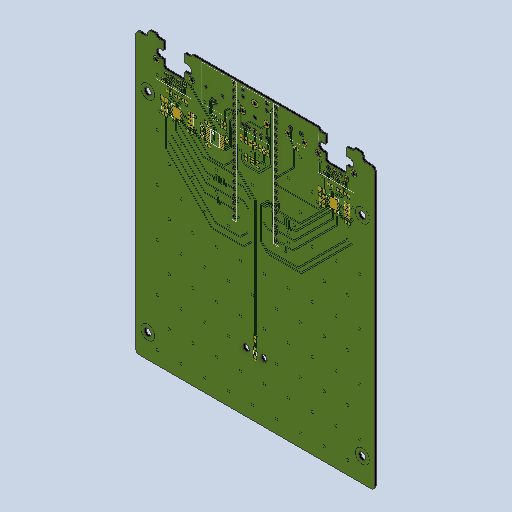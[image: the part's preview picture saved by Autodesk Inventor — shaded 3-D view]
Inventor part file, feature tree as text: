
AUTODESK INVENTOR PART (.ipt)
format: ipt  version: 2022.2 (Build 262287010, 287A)  size: 1,563,136 bytes
history: native  units: mm
features: hole x93, sketch x93, other x8, extrude x3
ambient origin geometry x8: Origin, YZ Plane, XZ Plane, XY Plane, X Axis, Y Axis, Z Axis, Center Point
bodies: Solid1 (feature_tree)
feature tree (197):
  other  "BaseBoard_BOARD"
  other  "BoardFrontPlane"
  extrude  "BoardOutline"  Depth=0.13mm TaperAngle=0.0deg
  hole  "J4-1"  [1 undecoded]
  hole  "J4-2"  [1 undecoded]
  hole  "J4-3"  [1 undecoded]
  hole  "J4-4"  [1 undecoded]
  hole  "J4-5"  [1 undecoded]
  hole  "J4-6"  [1 undecoded]
  hole  "J2-21"  [1 undecoded]
  hole  "J2-22"  [1 undecoded]
  hole  "J2-23"  [1 undecoded]
  hole  "J2-24"  [1 undecoded]
  hole  "J2-25"  [1 undecoded]
  hole  "J2-26"  [1 undecoded]
  hole  "J2-27"  [1 undecoded]
  hole  "J2-28"  [1 undecoded]
  hole  "J2-29"  [1 undecoded]
  hole  "J2-30"  [1 undecoded]
  hole  "J2-31"  [1 undecoded]
  hole  "J2-32"  [1 undecoded]
  hole  "J2-33"  [1 undecoded]
  hole  "J2-34"  [1 undecoded]
  hole  "J2-35"  [1 undecoded]
  hole  "J2-36"  [1 undecoded]
  hole  "J2-37"  [1 undecoded]
  hole  "J2-38"  [1 undecoded]
  hole  "J2-39"  [1 undecoded]
  hole  "J2-40"  [1 undecoded]
  hole  "J1-1"  [1 undecoded]
  hole  "J1-2"  [1 undecoded]
  hole  "J1-3"  [1 undecoded]
  hole  "J1-4"  [1 undecoded]
  hole  "J1-5"  [1 undecoded]
  hole  "J1-6"  [1 undecoded]
  hole  "J1-7"  [1 undecoded]
  hole  "J1-8"  [1 undecoded]
  hole  "J1-9"  [1 undecoded]
  hole  "J1-10"  [1 undecoded]
  hole  "J1-11"  [1 undecoded]
  hole  "J1-12"  [1 undecoded]
  hole  "J1-13"  [1 undecoded]
  hole  "J1-14"  [1 undecoded]
  hole  "J1-15"  [1 undecoded]
  hole  "J1-16"  [1 undecoded]
  hole  "J1-17"  [1 undecoded]
  hole  "J1-18"  [1 undecoded]
  hole  "J1-19"  [1 undecoded]
  hole  "J1-20"  [1 undecoded]
  extrude  "Cutout 1"  [1 undecoded]
  extrude  "Cutout 2"  [1 undecoded]
  other  "Decal_Top"
  other  "Decal_Bottom"
  hole  "J3-MH7"  [1 undecoded]
  hole  "J3-MH5"  [1 undecoded]
  hole  "J3-MH6"  [1 undecoded]
  hole  "J3-MH4"  [1 undecoded]
  hole  "J3-MH3"  [1 undecoded]
  hole  "J3-MH2"  [1 undecoded]
  hole  "J3-MH1"  [1 undecoded]
  hole  "J3-1"  [1 undecoded]
  hole  "J3-4"  [1 undecoded]
  hole  "J3-5"  [1 undecoded]
  hole  "J3-6"  [1 undecoded]
  hole  "J3-2"  [1 undecoded]
  hole  "J3-3"  [1 undecoded]
  hole  "J6-MH4"  [1 undecoded]
  hole  "J6-MH3"  [1 undecoded]
  hole  "J6-MH2"  [1 undecoded]
  hole  "J6-MH1"  [1 undecoded]
  hole  "J6-8"  [1 undecoded]
  hole  "J6-7"  [1 undecoded]
  hole  "J6-6"  [1 undecoded]
  hole  "J6-5"  [1 undecoded]
  hole  "J6-4"  [1 undecoded]
  hole  "J6-3"  [1 undecoded]
  hole  "J6-2"  [1 undecoded]
  hole  "J6-1"  [1 undecoded]
  hole  "J5-MH4"  [1 undecoded]
  hole  "J5-MH3"  [1 undecoded]
  hole  "J5-MH2"  [1 undecoded]
  hole  "J5-MH1"  [1 undecoded]
  hole  "J5-8"  [1 undecoded]
  hole  "J5-7"  [1 undecoded]
  hole  "J5-6"  [1 undecoded]
  hole  "J5-5"  [1 undecoded]
  hole  "J5-4"  [1 undecoded]
  hole  "J5-3"  [1 undecoded]
  hole  "J5-2"  [1 undecoded]
  hole  "J5-1"  [1 undecoded]
  hole  "Free-1_FEOXJPHT"  [1 undecoded]
  hole  "Free-1_SDAHNFJX"  [1 undecoded]
  hole  "Free-1_CCSYNVNB"  [1 undecoded]
  hole  "Free-1_NPNJQHMH"  [1 undecoded]
  hole  "Free-MH3"  [1 undecoded]
  hole  "Free-MH2"  [1 undecoded]
  hole  "S1-MH2"  [1 undecoded]
  hole  "S1-MH1"  [1 undecoded]
  hole  "S1-2"  [1 undecoded]
  hole  "S1-1"  [1 undecoded]
  sketch  "Sketch8"  dims[d0=0.798mm d1=0.0mm]
  sketch  "Sketch9"  dims[d34=0.6mm d35=6.0mm d36=4.0mm d37=2.0mm d38=90.0deg d39=8.0mm d40=0.0mm]
  sketch  "Sketch10"  dims[d41=0.6mm d42=6.0mm d43=4.0mm d44=2.0mm d45=90.0deg d46=8.0mm d47=0.0mm]
  sketch  "Sketch11"  dims[d48=0.6mm d49=6.0mm d50=4.0mm d51=2.0mm d52=90.0deg d53=8.0mm d54=0.0mm]
  sketch  "Sketch12"  dims[d55=0.6mm d56=6.0mm d57=4.0mm d58=2.0mm d59=90.0deg d60=8.0mm d61=0.0mm]
  sketch  "Sketch13"  dims[d62=1.0mm d63=6.0mm d64=4.0mm d65=2.0mm d66=90.0deg d67=8.0mm d68=0.0mm]
  sketch  "Sketch53"  dims[d69=1.0mm d70=6.0mm d71=4.0mm d72=2.0mm d73=90.0deg d74=8.0mm d75=0.0mm]
  sketch  "Sketch54"  dims[d304=1.04mm d305=6.0mm d306=4.0mm d307=2.0mm d308=90.0deg d309=8.0mm d310=0.0mm]
  sketch  "Sketch55"  dims[d311=1.04mm d312=6.0mm d313=4.0mm d314=2.0mm d315=90.0deg d316=8.0mm d317=0.0mm]
  sketch  "Sketch56"  dims[d318=1.04mm d319=6.0mm d320=4.0mm d321=2.0mm d322=90.0deg d323=8.0mm d324=0.0mm]
  sketch  "Sketch57"  dims[d325=1.04mm d326=6.0mm d327=4.0mm d328=2.0mm d329=90.0deg d330=8.0mm d331=0.0mm]
  sketch  "Sketch58"  dims[d332=1.04mm d333=6.0mm d334=4.0mm d335=2.0mm d336=90.0deg d337=8.0mm d338=0.0mm]
  sketch  "Sketch59"  dims[d339=1.04mm d340=6.0mm d341=4.0mm d342=2.0mm d343=90.0deg d344=8.0mm d345=0.0mm]
  sketch  "Sketch60"  dims[d346=1.04mm d347=6.0mm d348=4.0mm d349=2.0mm d350=90.0deg d351=8.0mm d352=0.0mm]
  sketch  "Sketch61"  dims[d353=1.04mm d354=6.0mm d355=4.0mm d356=2.0mm d357=90.0deg d358=8.0mm d359=0.0mm]
  sketch  "Sketch62"  dims[d360=1.04mm d361=6.0mm d362=4.0mm d363=2.0mm d364=90.0deg d365=8.0mm d366=0.0mm]
  sketch  "Sketch63"  dims[d367=1.04mm d368=6.0mm d369=4.0mm d370=2.0mm d371=90.0deg d372=8.0mm d373=0.0mm]
  sketch  "Sketch64"  dims[d374=1.04mm d375=6.0mm d376=4.0mm d377=2.0mm d378=90.0deg d379=8.0mm d380=0.0mm]
  sketch  "Sketch65"  dims[d381=1.04mm d382=6.0mm d383=4.0mm d384=2.0mm d385=90.0deg d386=8.0mm d387=0.0mm]
  sketch  "Sketch66"  dims[d388=1.04mm d389=6.0mm d390=4.0mm d391=2.0mm d392=90.0deg d393=8.0mm d394=0.0mm]
  sketch  "Sketch67"  dims[d395=1.04mm d396=6.0mm d397=4.0mm d398=2.0mm d399=90.0deg d400=8.0mm d401=0.0mm]
  sketch  "Sketch68"  dims[d402=1.04mm d403=6.0mm d404=4.0mm d405=2.0mm d406=90.0deg d407=8.0mm d408=0.0mm]
  sketch  "Sketch69"  dims[d409=1.04mm d410=6.0mm d411=4.0mm d412=2.0mm d413=90.0deg d414=8.0mm d415=0.0mm]
  sketch  "Sketch70"  dims[d416=1.04mm d417=6.0mm d418=4.0mm d419=2.0mm d420=90.0deg d421=8.0mm d422=0.0mm]
  sketch  "Sketch71"  dims[d423=1.04mm d424=6.0mm d425=4.0mm d426=2.0mm d427=90.0deg d428=8.0mm d429=0.0mm]
  sketch  "Sketch72"  dims[d430=1.04mm d431=6.0mm d432=4.0mm d433=2.0mm d434=90.0deg d435=8.0mm d436=0.0mm]
  sketch  "Sketch73"  dims[d437=1.04mm d438=6.0mm d439=4.0mm d440=2.0mm d441=90.0deg d442=8.0mm d443=0.0mm]
  sketch  "Sketch74"  dims[d444=1.04mm d445=6.0mm d446=4.0mm d447=2.0mm d448=90.0deg d449=8.0mm d450=0.0mm]
  sketch  "Sketch75"  dims[d451=1.04mm d452=6.0mm d453=4.0mm d454=2.0mm d455=90.0deg d456=8.0mm d457=0.0mm]
  sketch  "Sketch76"  dims[d458=1.04mm d459=6.0mm d460=4.0mm d461=2.0mm d462=90.0deg d463=8.0mm d464=0.0mm]
  sketch  "Sketch77"  dims[d465=1.04mm d466=6.0mm d467=4.0mm d468=2.0mm d469=90.0deg d470=8.0mm d471=0.0mm]
  sketch  "Sketch78"  dims[d472=1.04mm d473=6.0mm d474=4.0mm d475=2.0mm d476=90.0deg d477=8.0mm d478=0.0mm]
  sketch  "Sketch79"  dims[d479=1.04mm d480=6.0mm d481=4.0mm d482=2.0mm d483=90.0deg d484=8.0mm d485=0.0mm]
  sketch  "Sketch80"  dims[d486=1.04mm d487=6.0mm d488=4.0mm d489=2.0mm d490=90.0deg d491=8.0mm d492=0.0mm]
  sketch  "Sketch81"  dims[d493=1.04mm d494=6.0mm d495=4.0mm d496=2.0mm d497=90.0deg d498=8.0mm d499=0.0mm]
  sketch  "Sketch82"  dims[d500=1.04mm d501=6.0mm d502=4.0mm d503=2.0mm d504=90.0deg d505=8.0mm d506=0.0mm]
  sketch  "Sketch83"  dims[d507=1.04mm d508=6.0mm d509=4.0mm d510=2.0mm d511=90.0deg d512=8.0mm d513=0.0mm]
  sketch  "Sketch84"  dims[d514=1.04mm d515=6.0mm d516=4.0mm d517=2.0mm d518=90.0deg d519=8.0mm d520=0.0mm]
  sketch  "Sketch85"  dims[d521=1.04mm d522=6.0mm d523=4.0mm d524=2.0mm d525=90.0deg d526=8.0mm d527=0.0mm]
  sketch  "Sketch86"  dims[d528=1.04mm d529=6.0mm d530=4.0mm d531=2.0mm d532=90.0deg d533=8.0mm d534=0.0mm]
  sketch  "Sketch87"  dims[d535=1.04mm d536=6.0mm d537=4.0mm d538=2.0mm d539=90.0deg d540=8.0mm d541=0.0mm]
  sketch  "Sketch88"  dims[d542=1.04mm d543=6.0mm d544=4.0mm d545=2.0mm d546=90.0deg d547=8.0mm d548=0.0mm]
  sketch  "Sketch89"  dims[d549=1.04mm d550=6.0mm d551=4.0mm d552=2.0mm d553=90.0deg d554=8.0mm d555=0.0mm]
  sketch  "Sketch90"  dims[d556=1.04mm d557=6.0mm d558=4.0mm d559=2.0mm d560=90.0deg d561=8.0mm d562=0.0mm]
  sketch  "Sketch91"  dims[d563=1.04mm d564=6.0mm d565=4.0mm d566=2.0mm d567=90.0deg d568=8.0mm d569=0.0mm]
  sketch  "Sketch92"  dims[d570=1.04mm d571=6.0mm d572=4.0mm d573=2.0mm d574=90.0deg d575=8.0mm d576=0.0mm]
  other  "img_Top"
  other  "G_-980059402_TopDecalImage"
  other  "img_Bottom"
  other  "G_-980059402_BottomDecalImage"
  sketch  "Sketch155"  dims[d577=1.04mm d578=6.0mm d579=4.0mm d580=2.0mm d581=90.0deg d582=8.0mm d583=0.0mm d846=0.13mm d847=0.0mm]
  sketch  "Sketch156"  dims[d922=0.13mm d923=0.0mm d924=0.798mm]
  sketch  "Sketch157"  dims[d926=-0.798mm]
  sketch  "Sketch158"  dims[d928=1.2mm d929=6.0mm d930=4.0mm d931=2.0mm d932=90.0deg d933=8.0mm d934=0.0mm]
  sketch  "Sketch159"  dims[d935=1.2mm d936=6.0mm d937=4.0mm d938=2.0mm d939=90.0deg d940=8.0mm d941=0.0mm]
  sketch  "Sketch160"  dims[d942=1.2mm d943=6.0mm d944=4.0mm d945=2.0mm d946=90.0deg d947=8.0mm d948=0.0mm]
  sketch  "Sketch161"  dims[d949=1.2mm d950=6.0mm d951=4.0mm d952=2.0mm d953=90.0deg d954=8.0mm d955=0.0mm]
  sketch  "Sketch162"  dims[d956=1.2mm d957=6.0mm d958=4.0mm d959=2.0mm d960=90.0deg d961=8.0mm d962=0.0mm]
  sketch  "Sketch163"  dims[d963=1.2mm d964=6.0mm d965=4.0mm d966=2.0mm d967=90.0deg d968=8.0mm d969=0.0mm]
  sketch  "Sketch164"  dims[d970=1.2mm d971=6.0mm d972=4.0mm d973=2.0mm d974=90.0deg d975=8.0mm d976=0.0mm]
  sketch  "Sketch165"  dims[d977=1.4mm d978=6.0mm d979=4.0mm d980=2.0mm d981=90.0deg d982=8.0mm d983=0.0mm]
  sketch  "Sketch166"  dims[d984=1.0mm d985=6.0mm d986=4.0mm d987=2.0mm d988=90.0deg d989=8.0mm d990=0.0mm]
  sketch  "Sketch167"  dims[d991=1.0mm d992=6.0mm d993=4.0mm d994=2.0mm d995=90.0deg d996=8.0mm d997=0.0mm]
  sketch  "Sketch168"  dims[d998=1.0mm d999=6.0mm d1000=4.0mm d1001=2.0mm d1002=90.0deg d1003=8.0mm d1004=0.0mm]
  sketch  "Sketch169"  dims[d1005=1.4mm d1006=6.0mm d1007=4.0mm d1008=2.0mm d1009=90.0deg d1010=8.0mm d1011=0.0mm]
  sketch  "Sketch170"  dims[d1012=1.4mm d1013=6.0mm d1014=4.0mm d1015=2.0mm d1016=90.0deg d1017=8.0mm d1018=0.0mm]
  sketch  "Sketch171"  dims[d1019=3.26mm d1020=6.0mm d1021=4.0mm d1022=2.0mm d1023=90.0deg d1024=8.0mm d1025=0.0mm]
  sketch  "Sketch172"  dims[d1026=3.26mm d1027=6.0mm d1028=4.0mm d1029=2.0mm d1030=90.0deg d1031=8.0mm d1032=0.0mm]
  sketch  "Sketch173"  dims[d1033=1.5mm d1034=6.0mm d1035=4.0mm d1036=2.0mm d1037=90.0deg d1038=8.0mm d1039=0.0mm]
  sketch  "Sketch174"  dims[d1040=1.5mm d1041=6.0mm d1042=4.0mm d1043=2.0mm d1044=90.0deg d1045=8.0mm d1046=0.0mm]
  sketch  "Sketch175"  dims[d1047=0.89mm d1048=6.0mm d1049=4.0mm d1050=2.0mm d1051=90.0deg d1052=8.0mm d1053=0.0mm]
  sketch  "Sketch176"  dims[d1054=0.89mm d1055=6.0mm d1056=4.0mm d1057=2.0mm d1058=90.0deg d1059=8.0mm d1060=0.0mm]
  sketch  "Sketch177"  dims[d1061=0.89mm d1062=6.0mm d1063=4.0mm d1064=2.0mm d1065=90.0deg d1066=8.0mm d1067=0.0mm]
  sketch  "Sketch178"  dims[d1068=0.89mm d1069=6.0mm d1070=4.0mm d1071=2.0mm d1072=90.0deg d1073=8.0mm d1074=0.0mm]
  sketch  "Sketch179"  dims[d1075=0.89mm d1076=6.0mm d1077=4.0mm d1078=2.0mm d1079=90.0deg d1080=8.0mm d1081=0.0mm]
  sketch  "Sketch180"  dims[d1082=0.89mm d1083=6.0mm d1084=4.0mm d1085=2.0mm d1086=90.0deg d1087=8.0mm d1088=0.0mm]
  sketch  "Sketch181"  dims[d1089=0.89mm d1090=6.0mm d1091=4.0mm d1092=2.0mm d1093=90.0deg d1094=8.0mm d1095=0.0mm]
  sketch  "Sketch182"  dims[d1096=0.89mm d1097=6.0mm d1098=4.0mm d1099=2.0mm d1100=90.0deg d1101=8.0mm d1102=0.0mm]
  sketch  "Sketch183"  dims[d1103=3.26mm d1104=6.0mm d1105=4.0mm d1106=2.0mm d1107=90.0deg d1108=8.0mm d1109=0.0mm]
  sketch  "Sketch184"  dims[d1110=3.26mm d1111=6.0mm d1112=4.0mm d1113=2.0mm d1114=90.0deg d1115=8.0mm d1116=0.0mm]
  sketch  "Sketch185"  dims[d1117=1.5mm d1118=6.0mm d1119=4.0mm d1120=2.0mm d1121=90.0deg d1122=8.0mm d1123=0.0mm]
  sketch  "Sketch186"  dims[d1124=1.5mm d1125=6.0mm d1126=4.0mm d1127=2.0mm d1128=90.0deg d1129=8.0mm d1130=0.0mm]
  sketch  "Sketch187"  dims[d1131=0.89mm d1132=6.0mm d1133=4.0mm d1134=2.0mm d1135=90.0deg d1136=8.0mm d1137=0.0mm]
  sketch  "Sketch188"  dims[d1138=0.89mm d1139=6.0mm d1140=4.0mm d1141=2.0mm d1142=90.0deg d1143=8.0mm d1144=0.0mm]
  sketch  "Sketch189"  dims[d1145=0.89mm d1146=6.0mm d1147=4.0mm d1148=2.0mm d1149=90.0deg d1150=8.0mm d1151=0.0mm]
  sketch  "Sketch190"  dims[d1152=0.89mm d1153=6.0mm d1154=4.0mm d1155=2.0mm d1156=90.0deg d1157=8.0mm d1158=0.0mm]
  sketch  "Sketch191"  dims[d1159=0.89mm d1160=6.0mm d1161=4.0mm d1162=2.0mm d1163=90.0deg d1164=8.0mm d1165=0.0mm]
  sketch  "Sketch192"  dims[d1166=0.89mm d1167=6.0mm d1168=4.0mm d1169=2.0mm d1170=90.0deg d1171=8.0mm d1172=0.0mm]
  sketch  "Sketch193"  dims[d1173=0.89mm d1174=6.0mm d1175=4.0mm d1176=2.0mm d1177=90.0deg d1178=8.0mm d1179=0.0mm]
  sketch  "Sketch194"  dims[d1180=0.89mm d1181=6.0mm d1182=4.0mm d1183=2.0mm d1184=90.0deg d1185=8.0mm d1186=0.0mm]
  sketch  "Sketch195"  dims[d1187=3.0mm d1188=6.0mm d1189=4.0mm d1190=2.0mm d1191=90.0deg d1192=8.0mm d1193=0.0mm]
  sketch  "Sketch196"  dims[d1194=3.0mm d1195=6.0mm d1196=4.0mm d1197=2.0mm d1198=90.0deg d1199=8.0mm d1200=0.0mm]
  sketch  "Sketch197"  dims[d1201=3.0mm d1202=6.0mm d1203=4.0mm d1204=2.0mm d1205=90.0deg d1206=8.0mm d1207=0.0mm]
  sketch  "Sketch198"  dims[d1208=3.0mm d1209=6.0mm d1210=4.0mm d1211=2.0mm d1212=90.0deg d1213=8.0mm d1214=0.0mm]
  sketch  "Sketch199"  dims[d1215=2.5mm d1216=6.0mm d1217=4.0mm d1218=2.0mm d1219=90.0deg d1220=8.0mm d1221=0.0mm]
  sketch  "Sketch200"  dims[d1222=2.5mm d1223=6.0mm d1224=4.0mm d1225=2.0mm d1226=90.0deg d1227=8.0mm d1228=0.0mm]
  sketch  "Sketch201"  dims[d1229=1.3mm d1230=6.0mm d1231=4.0mm d1232=2.0mm d1233=90.0deg d1234=8.0mm d1235=0.0mm d1236=1.3mm d1237=6.0mm d1238=4.0mm d1239=2.0mm d1240=90.0deg d1241=8.0mm d1242=0.0mm d1243=1.0mm d1244=6.0mm d1245=4.0mm d1246=2.0mm d1247=90.0deg d1248=8.0mm d1249=0.0mm d1250=1.0mm d1251=6.0mm d1252=4.0mm d1253=2.0mm d1254=90.0deg d1255=8.0mm d1256=0.0mm]
note: 95 required parameter values undecoded (feature->parameter linkage not recoverable at this tier; creation-order binding heuristic only, values carry confidence <= 0.55)
